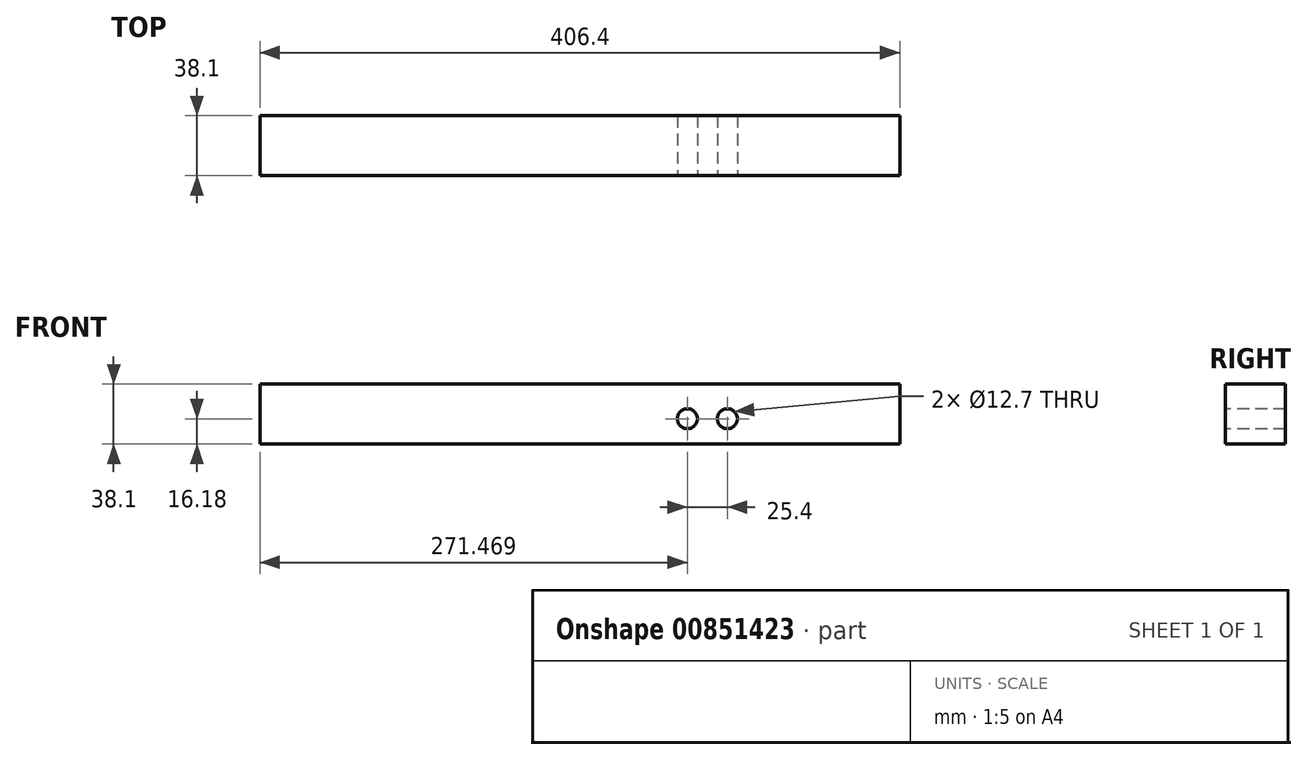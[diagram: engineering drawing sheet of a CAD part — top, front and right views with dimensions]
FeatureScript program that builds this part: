
annotation { "Feature Type Name" : "Feature", "Feature Type Description" : "" }
export const myFeature = defineFeature(function(context is Context, id is Id, definition is map)
    precondition{}
    {
        {
            var Q0;
            Q0=qCreatedBy(makeId("Front.planeOp"),FACE);
            var sketch = newSketch(context, id + "F0", { "sketchPlane" : qUnion([Q0])});
            skLineSegment(sketch, "E0", {"start": v(155.7, 21.92) * mm, "end": v(-250.7, 21.92) * mm});
            skLineSegment(sketch, "E1", {"start": v(-250.7, 21.92) * mm, "end": v(-250.7, -16.18) * mm});
            skLineSegment(sketch, "E2", {"start": v(155.7, 21.92) * mm, "end": v(155.7, -16.18) * mm});
            skLineSegment(sketch, "E3", {"start": v(-250.7, -16.18) * mm, "end": v(155.7, -16.18) * mm});
            skSolve(sketch);
        }
        {
            var Q0;
            Q0 = qSketchRegion(id + "F0", true);
            extrude(context, id + "F1", {"entities" : qUnion([Q0]), "depth" : 38.1 * mm, "offsetDistance" : 25.4 * mm});
        }
        {
            var Q0;
            Q0=makeQuery(id+"F1.opExtrude","CAP_FACE",FACE,{"disambiguationData":[OSD([sQuery(id+"F0.wireOp",EDGE,"E0"),sQuery(id+"F0.wireOp",EDGE,"E1"),sQuery(id+"F0.wireOp",EDGE,"E2"),sQuery(id+"F0.wireOp",EDGE,"E3")])],"isStart":false});
            var sketch = newSketch(context, id + "F2", { "sketchPlane" : qUnion([Q0])});
            skCircle(sketch, "E4", {"center": v(20.78, 0) * mm, "radius": 6.35 * mm});
            skCircle(sketch, "E5", {"center": v(46.18, 0) * mm, "radius": 6.35 * mm});
            skSolve(sketch);
        }
        {
            var Q0;
            Q0 = qSketchRegion(id + "F2", true);
            extrude(context, id + "F3", {"entities" : qUnion([Q0]), "operationType" : NewBodyOperationType.REMOVE, "oppositeDirection" : true, "depth" : 50.8 * mm, "offsetDistance" : 25.4 * mm});
        }
    });
